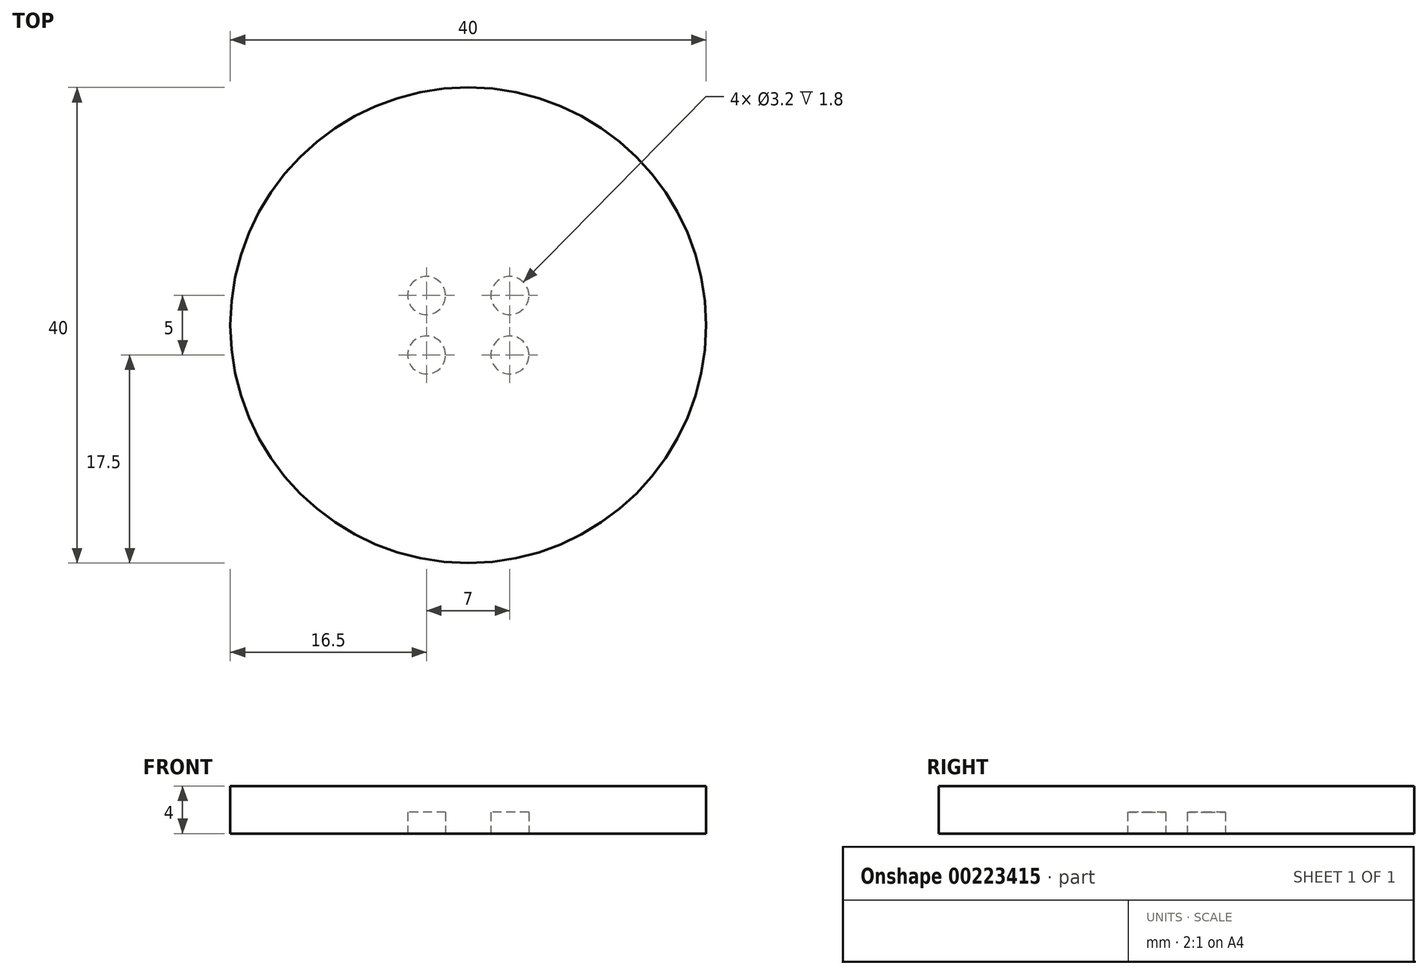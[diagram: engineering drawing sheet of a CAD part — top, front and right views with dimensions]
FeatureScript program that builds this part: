
annotation { "Feature Type Name" : "Feature", "Feature Type Description" : "" }
export const myFeature = defineFeature(function(context is Context, id is Id, definition is map)
    precondition{}
    {
        {
            var Q0;
            Q0=qCreatedBy(makeId("Top.planeOp"),FACE);
            var sketch = newSketch(context, id + "F0", { "sketchPlane" : qUnion([Q0])});
            skCircle(sketch, "E0", {"center": v(0, 0) * mm, "radius": 20 * mm});
            skLineSegment(sketch, "E1.bottom", {"start": v(3.5, -2.5) * mm, "end": v(-3.5, -2.5) * mm, "construction": true});
            skLineSegment(sketch, "E1.top", {"start": v(3.5, 2.5) * mm, "end": v(-3.5, 2.5) * mm, "construction": true});
            skLineSegment(sketch, "E1.left", {"start": v(3.5, -2.5) * mm, "end": v(3.5, 2.5) * mm, "construction": true});
            skLineSegment(sketch, "E1.right", {"start": v(-3.5, -2.5) * mm, "end": v(-3.5, 2.5) * mm, "construction": true});
            skCircle(sketch, "E2", {"center": v(-3.5, 2.5) * mm, "radius": 1.6 * mm});
            skCircle(sketch, "E3", {"center": v(3.5, 2.5) * mm, "radius": 1.6 * mm});
            skCircle(sketch, "E4", {"center": v(3.5, -2.5) * mm, "radius": 1.6 * mm});
            skCircle(sketch, "E5", {"center": v(-3.5, -2.5) * mm, "radius": 1.6 * mm});
            skSolve(sketch);
        }
        {
            var Q0;
            Q0=makeQuery(id+"F0.imprint","IMPRINT",FACE,{"disambiguationData":[TD([[makeQuery(id+"F0.imprint","IMPRINT",EDGE,{"derivedFrom":sQuery(id+"F0.wireOp",EDGE,"E3")}),1.0]])]});
            var Q1;
            Q1=makeQuery(id+"F0.imprint","IMPRINT",FACE,{"disambiguationData":[TD([[makeQuery(id+"F0.imprint","IMPRINT",EDGE,{"derivedFrom":sQuery(id+"F0.wireOp",EDGE,"E2")}),1.0]])]});
            var Q2;
            Q2=makeQuery(id+"F0.imprint","IMPRINT",FACE,{"disambiguationData":[TD([[makeQuery(id+"F0.imprint","IMPRINT",EDGE,{"derivedFrom":sQuery(id+"F0.wireOp",EDGE,"E0")}),1.0]])]});
            var Q3;
            Q3=makeQuery(id+"F0.imprint","IMPRINT",FACE,{"disambiguationData":[TD([[makeQuery(id+"F0.imprint","IMPRINT",EDGE,{"derivedFrom":sQuery(id+"F0.wireOp",EDGE,"E4")}),1.0]])]});
            var Q4;
            Q4=makeQuery(id+"F0.imprint","IMPRINT",FACE,{"disambiguationData":[TD([[makeQuery(id+"F0.imprint","IMPRINT",EDGE,{"derivedFrom":sQuery(id+"F0.wireOp",EDGE,"E5")}),1.0]])]});
            extrude(context, id + "F1", {"entities" : qUnion([Q0, Q1, Q2, Q3, Q4]), "depth" : 4 * mm});
        }
        {
            var Q0;
            Q0=makeQuery(id+"F0.imprint","IMPRINT",FACE,{"disambiguationData":[TD([[makeQuery(id+"F0.imprint","IMPRINT",EDGE,{"derivedFrom":sQuery(id+"F0.wireOp",EDGE,"E2")}),1.0]])]});
            var Q1;
            Q1=makeQuery(id+"F0.imprint","IMPRINT",FACE,{"disambiguationData":[TD([[makeQuery(id+"F0.imprint","IMPRINT",EDGE,{"derivedFrom":sQuery(id+"F0.wireOp",EDGE,"E5")}),1.0]])]});
            var Q2;
            Q2=makeQuery(id+"F0.imprint","IMPRINT",FACE,{"disambiguationData":[TD([[makeQuery(id+"F0.imprint","IMPRINT",EDGE,{"derivedFrom":sQuery(id+"F0.wireOp",EDGE,"E4")}),1.0]])]});
            var Q3;
            Q3=makeQuery(id+"F0.imprint","IMPRINT",FACE,{"disambiguationData":[TD([[makeQuery(id+"F0.imprint","IMPRINT",EDGE,{"derivedFrom":sQuery(id+"F0.wireOp",EDGE,"E3")}),1.0]])]});
            extrude(context, id + "F2", {"entities" : qUnion([Q0, Q1, Q2, Q3]), "operationType" : NewBodyOperationType.REMOVE, "depth" : 1.8 * mm});
        }
    });
